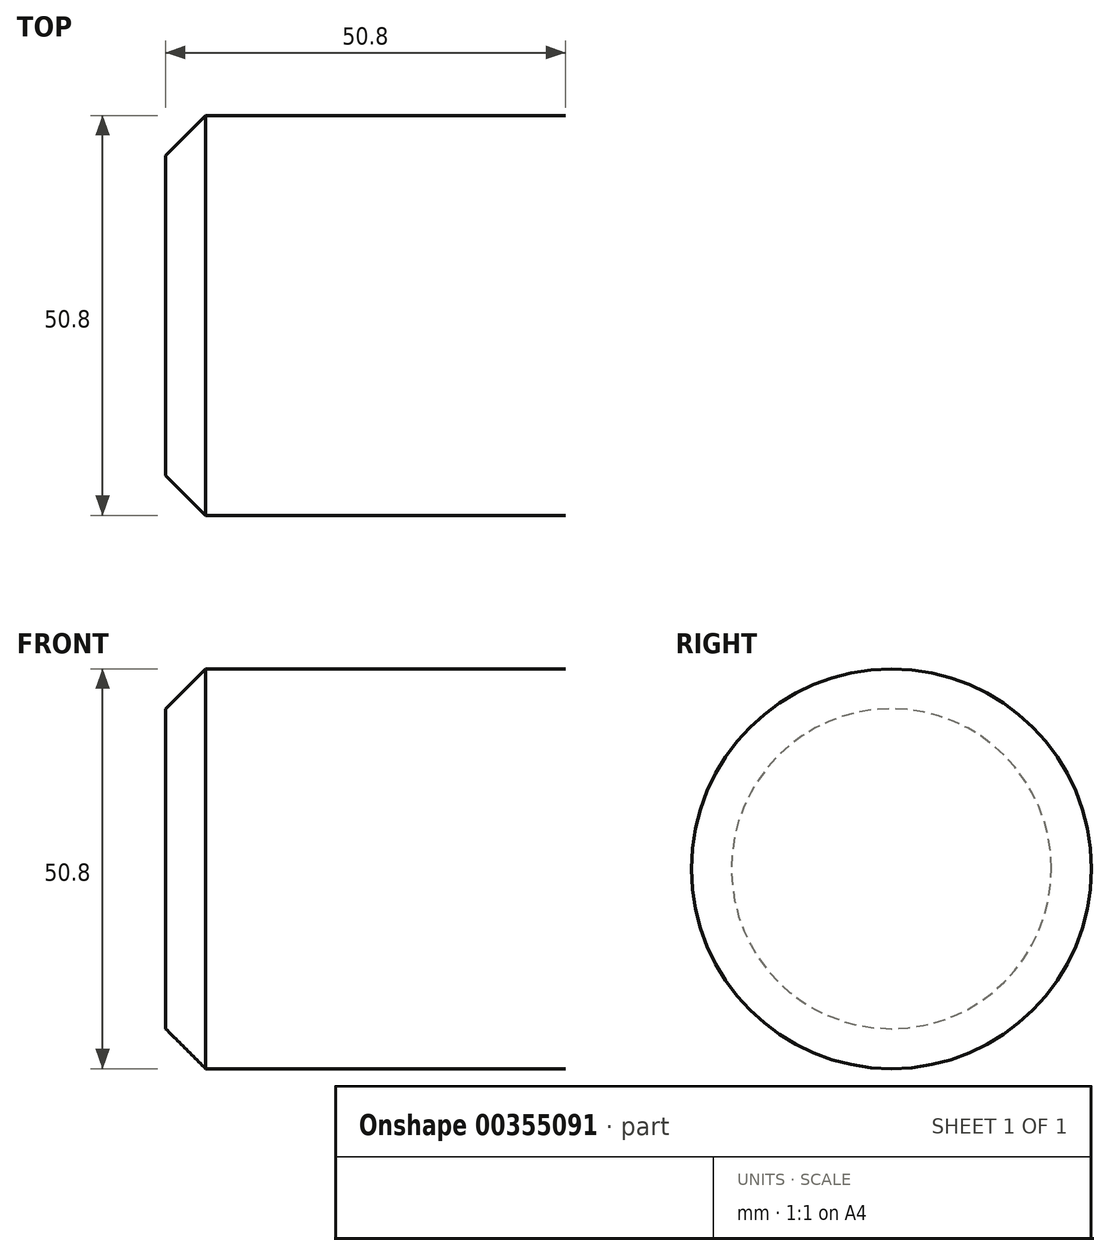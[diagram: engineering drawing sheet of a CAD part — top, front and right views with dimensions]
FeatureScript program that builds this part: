
annotation { "Feature Type Name" : "Feature", "Feature Type Description" : "" }
export const myFeature = defineFeature(function(context is Context, id is Id, definition is map)
    precondition{}
    {
        {
            var Q0;
            Q0=qCreatedBy(makeId("Top.planeOp"),FACE);
            var sketch = newSketch(context, id + "F0", { "sketchPlane" : qUnion([Q0])});
            skLineSegment(sketch, "E0.bottom", {"start": v(0, 0) * mm, "end": v(50.8, 0) * mm});
            skLineSegment(sketch, "E0.top", {"start": v(0, 25.4) * mm, "end": v(50.8, 25.4) * mm});
            skLineSegment(sketch, "E0.left", {"start": v(0, 0) * mm, "end": v(0, 25.4) * mm});
            skArc(sketch, "E1", {"start": v(50.8, 0) * mm, "mid": v(63.5, 12.7) * mm, "end": v(50.8, 25.4) * mm});
            skSolve(sketch);
        }
        {
            var Q0;
            Q0=makeQuery(id+"F0.imprint","IMPRINT",FACE,{"disambiguationData":[TD([[makeQuery(id+"F0.imprint","IMPRINT",EDGE,{"derivedFrom":sQuery(id+"F0.wireOp",EDGE,"E0.bottom")}),1.0]])]});
            var Q1;
            Q1=sQuery(id+"F0.wireOp",EDGE,"E0.top");
            revolve(context, id + "F1", {"entities" : qUnion([Q0]), "axis" : qUnion([Q1]), "revolveType" : RevolveType.FULL});
        }
        {
            var Q0;
            Q0=makeQuery(id+"F1.opRevolve","SWEPT_EDGE",EDGE,{"disambiguationData":[OSD([sQuery(id+"F0.wireOp",EDGE,"E0.bottom"),sQuery(id+"F0.wireOp",EDGE,"E0.left")])]});
            chamfer(context, id + "F2", {"entities" : qUnion([Q0]), "width" : 5.08 * mm, "tangentPropagation" : true});
        }
    });
